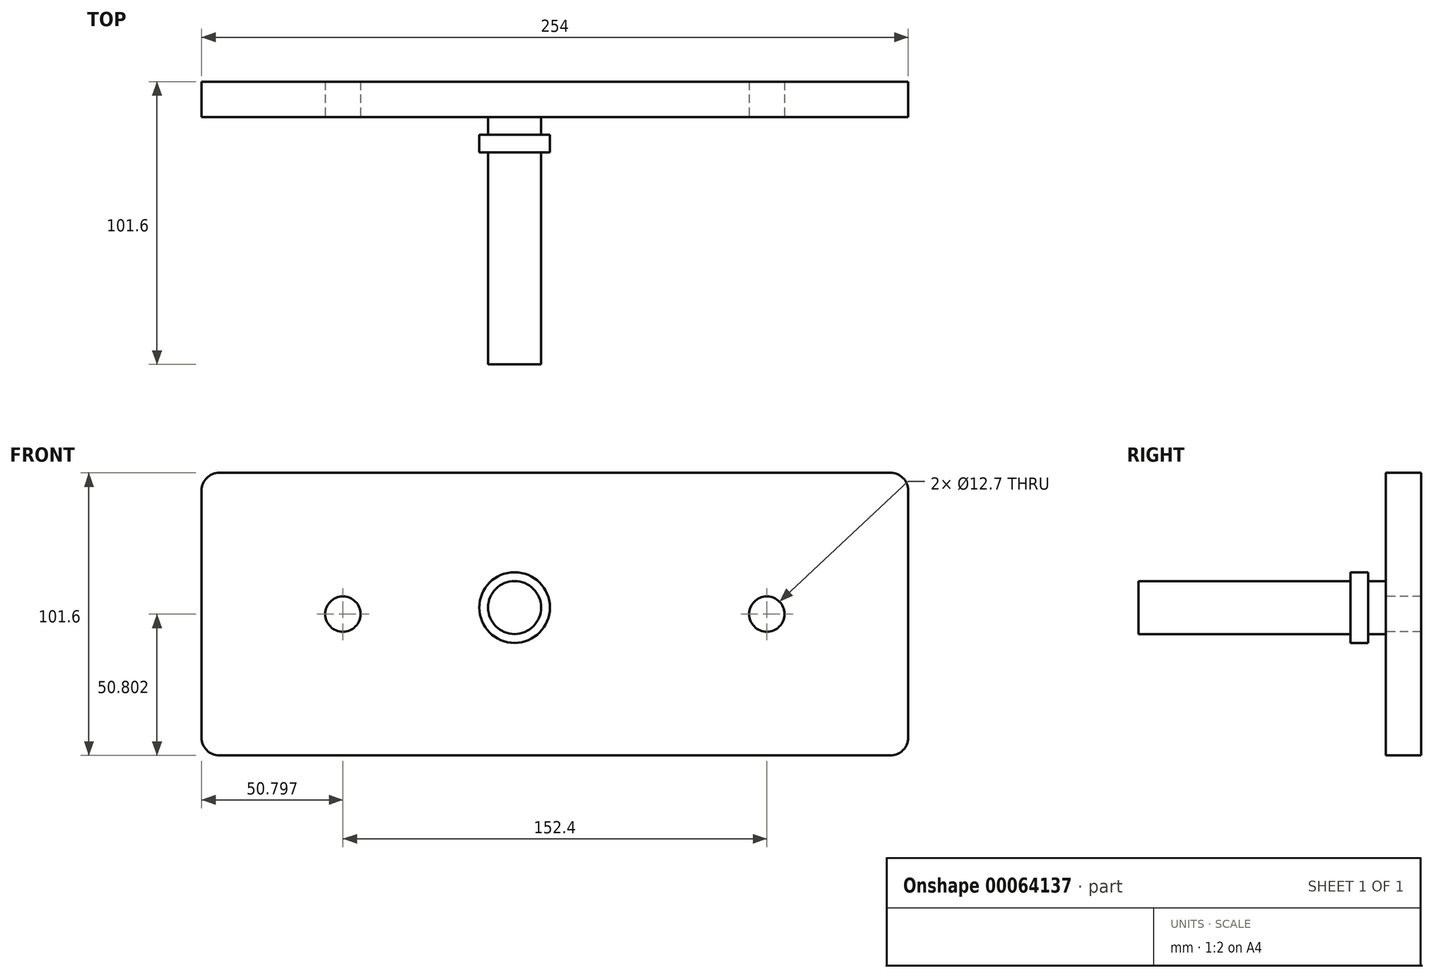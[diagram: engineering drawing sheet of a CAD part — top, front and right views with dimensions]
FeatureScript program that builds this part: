
annotation { "Feature Type Name" : "Feature", "Feature Type Description" : "" }
export const myFeature = defineFeature(function(context is Context, id is Id, definition is map)
    precondition{}
    {
        {
            var Q0;
            Q0=qCreatedBy(makeId("Front.planeOp"),FACE);
            var sketch = newSketch(context, id + "F0", { "sketchPlane" : qUnion([Q0])});
            skLineSegment(sketch, "E0.bottom", {"start": v(-112.51, -53.16) * mm, "end": v(141.49, -53.16) * mm});
            skLineSegment(sketch, "E0.top", {"start": v(-112.51, 48.44) * mm, "end": v(141.49, 48.44) * mm});
            skLineSegment(sketch, "E0.left", {"start": v(-112.51, -53.16) * mm, "end": v(-112.51, 48.44) * mm});
            skLineSegment(sketch, "E0.right", {"start": v(141.49, -53.16) * mm, "end": v(141.49, 48.44) * mm});
            skSolve(sketch);
        }
        {
            var Q0;
            Q0 = qSketchRegion(id + "F0", true);
            extrude(context, id + "F1", {"entities" : qUnion([Q0]), "depth" : 12.7 * mm});
        }
        {
            var Q0;
            Q0=makeQuery(id+"F1.opExtrude","CAP_FACE",FACE,{"disambiguationData":[OSD([sQuery(id+"F0.wireOp",EDGE,"E0.bottom"),sQuery(id+"F0.wireOp",EDGE,"E0.top"),sQuery(id+"F0.wireOp",EDGE,"E0.left"),sQuery(id+"F0.wireOp",EDGE,"E0.right")])],"isStart":false});
            var sketch = newSketch(context, id + "F2", { "sketchPlane" : qUnion([Q0])});
            skPoint(sketch, "E1", {"position": v(-61.71, -2.36) * mm});
            skPoint(sketch, "E1.positionSnap0", {"position": v(-112.51, -2.36) * mm});
            skPoint(sketch, "E2", {"position": v(90.69, -2.36) * mm});
            skSolve(sketch);
        }
        {
            var Q0;
            Q0=sQuery(id+"F2.wireOp",VERTEX,"E1");
            var Q1;
            Q1=sQuery(id+"F2.wireOp",VERTEX,"E2");
            var Q2;
            Q2=makeQuery(id+"F1.opExtrude","SWEPT_BODY",BODY,{"disambiguationData":[OSD([sQuery(id+"F0.wireOp",EDGE,"E0.bottom"),sQuery(id+"F0.wireOp",EDGE,"E0.top"),sQuery(id+"F0.wireOp",EDGE,"E0.left"),sQuery(id+"F0.wireOp",EDGE,"E0.right")])]});
            hole(context, id + "F3", {"style" : HoleStyle.SIMPLE, "holeDiameter" : 12.7 * mm, "endStyle" : HoleEndStyle.THROUGH, "locations" : qUnion([Q0, Q1]), "scope" : qUnion([Q2])});
        }
        {
            var Q0;
            Q0=makeQuery(id+"F1.opExtrude","SWEPT_EDGE",EDGE,{"disambiguationData":[OSD([sQuery(id+"F0.wireOp",EDGE,"E0.top"),sQuery(id+"F0.wireOp",EDGE,"E0.left")])]});
            var Q1;
            Q1=makeQuery(id+"F1.opExtrude","SWEPT_EDGE",EDGE,{"disambiguationData":[OSD([sQuery(id+"F0.wireOp",EDGE,"E0.bottom"),sQuery(id+"F0.wireOp",EDGE,"E0.left")])]});
            var Q2;
            Q2=makeQuery(id+"F1.opExtrude","SWEPT_EDGE",EDGE,{"disambiguationData":[OSD([sQuery(id+"F0.wireOp",EDGE,"E0.top"),sQuery(id+"F0.wireOp",EDGE,"E0.right")])]});
            var Q3;
            Q3=makeQuery(id+"F1.opExtrude","SWEPT_EDGE",EDGE,{"disambiguationData":[OSD([sQuery(id+"F0.wireOp",EDGE,"E0.bottom"),sQuery(id+"F0.wireOp",EDGE,"E0.right")])]});
            fillet(context, id + "F4", {"entities" : qUnion([Q0, Q1, Q2, Q3]), "radius" : 6.35 * mm, "tangentPropagation" : true, "allowEdgeOverflow" : false});
        }
        {
            var Q0;
            Q0=qCreatedBy(makeId("Front.planeOp"),FACE);
            var sketch = newSketch(context, id + "F5", { "sketchPlane" : qUnion([Q0])});
            skCircle(sketch, "E3", {"center": v(0, 0) * mm, "radius": 12.7 * mm});
            skSolve(sketch);
        }
        {
            var Q0;
            Q0=makeQuery(id+"F5.imprint","IMPRINT",FACE,{"disambiguationData":[TD([[makeQuery(id+"F5.imprint","IMPRINT",EDGE,{"derivedFrom":sQuery(id+"F5.wireOp",EDGE,"E3")}),1.0]])]});
            extrude(context, id + "F6", {"entities" : qUnion([Q0]), "depth" : 6.35 * mm});
        }
        {
            var Q0;
            Q0=makeQuery(id+"F6.opExtrude","CAP_FACE",FACE,{"disambiguationData":[OSD([sQuery(id+"F5.wireOp",EDGE,"E3")])],"isStart":false});
            var sketch = newSketch(context, id + "F7", { "sketchPlane" : qUnion([Q0])});
            skCircle(sketch, "E4", {"center": v(0, 0) * mm, "radius": 9.53 * mm});
            skSolve(sketch);
        }
        {
            var Q0;
            Q0=makeQuery(id+"F7.imprint","IMPRINT",FACE,{"disambiguationData":[TD([[makeQuery(id+"F7.imprint","IMPRINT",EDGE,{"derivedFrom":sQuery(id+"F7.wireOp",EDGE,"E4")}),1.0]])]});
            extrude(context, id + "F8", {"entities" : qUnion([Q0]), "operationType" : NewBodyOperationType.ADD, "depth" : 12.7 * mm});
        }
        {
            var Q0;
            Q0=makeQuery(id+"F8.opExtrude","CAP_FACE",FACE,{"disambiguationData":[OSD([sQuery(id+"F7.wireOp",EDGE,"E4")])],"isStart":false});
            var sketch = newSketch(context, id + "F9", { "sketchPlane" : qUnion([Q0])});
            skCircle(sketch, "E5.0", {"center": v(0, 0) * mm, "radius": 12.7 * mm});
            skSolve(sketch);
        }
        {
            var Q0;
            Q0 = qSketchRegion(id + "F9", true);
            extrude(context, id + "F10", {"entities" : qUnion([Q0]), "operationType" : NewBodyOperationType.ADD, "depth" : 6.35 * mm});
        }
        {
            var Q0;
            Q0=qCreatedBy(makeId("Front.planeOp"),FACE);
            var sketch = newSketch(context, id + "F11", { "sketchPlane" : qUnion([Q0])});
            skCircle(sketch, "E6", {"center": v(0, 0) * mm, "radius": 6.35 * mm});
            skSolve(sketch);
        }
        {
            var Q0;
            Q0 = qSketchRegion(id + "F11", true);
            extrude(context, id + "F12", {"entities" : qUnion([Q0]), "depth" : 25.4 * mm});
        }
        {
            var Q0;
            Q0=makeQuery(id+"F12.opExtrude","CAP_FACE",FACE,{"disambiguationData":[OSD([sQuery(id+"F11.wireOp",EDGE,"E6")])],"isStart":false});
            var sketch = newSketch(context, id + "F13", { "sketchPlane" : qUnion([Q0])});
            skCircle(sketch, "E7", {"center": v(0, 0) * mm, "radius": 9.53 * mm});
            skSolve(sketch);
        }
        {
            var Q0;
            Q0 = qSketchRegion(id + "F13", true);
            extrude(context, id + "F14", {"entities" : qUnion([Q0]), "operationType" : NewBodyOperationType.ADD, "depth" : 76.2 * mm});
        }
    });
